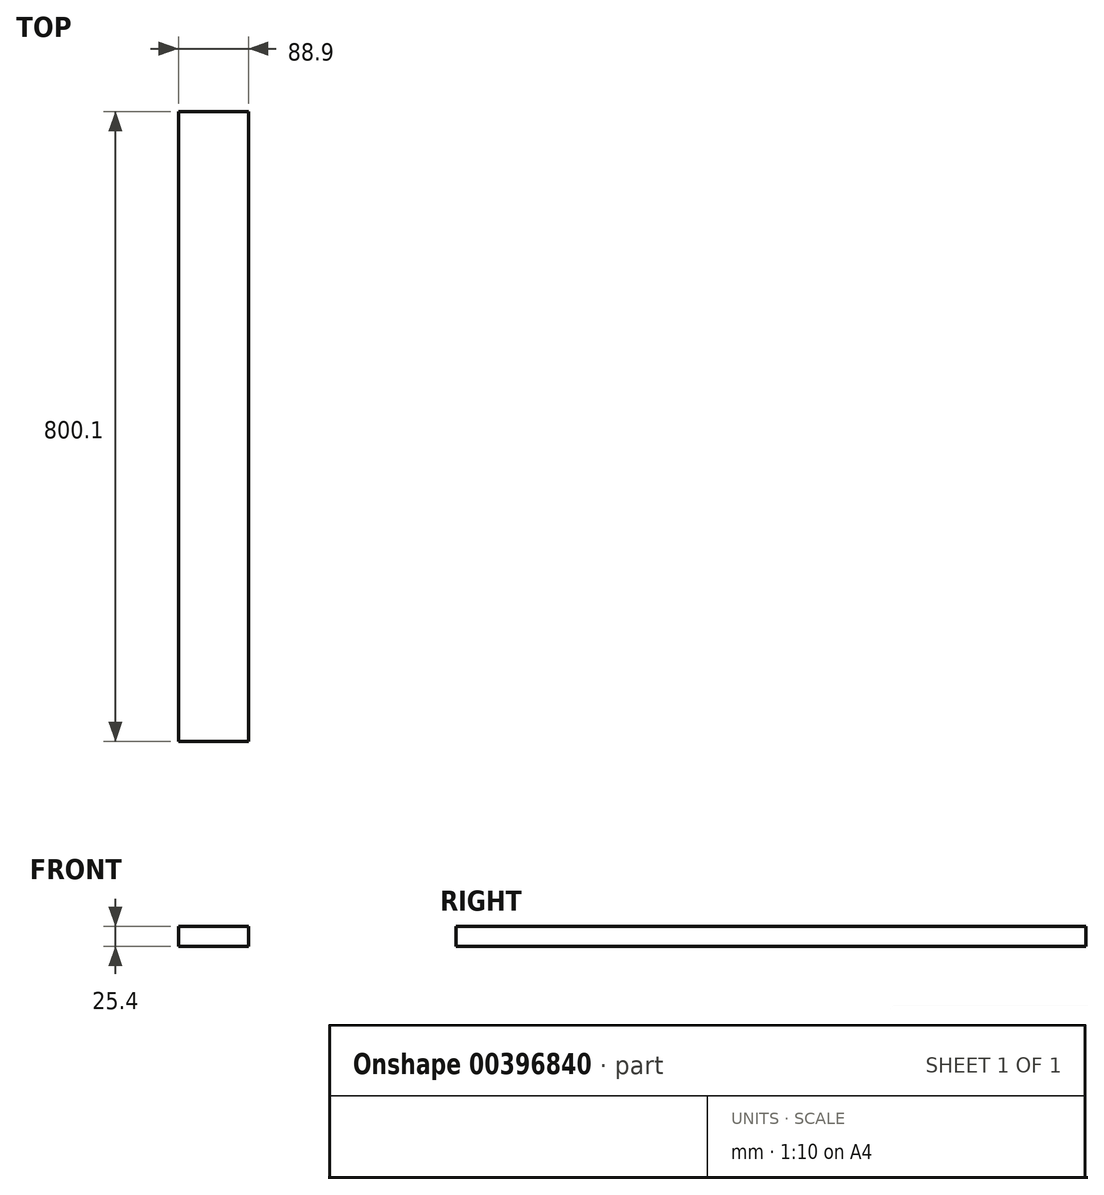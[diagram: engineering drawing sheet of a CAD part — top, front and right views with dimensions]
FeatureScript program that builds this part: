
annotation { "Feature Type Name" : "Feature", "Feature Type Description" : "" }
export const myFeature = defineFeature(function(context is Context, id is Id, definition is map)
    precondition{}
    {
        {
            var Q0;
            Q0=qCreatedBy(makeId("Top.planeOp"),FACE);
            var sketch = newSketch(context, id + "F0", { "sketchPlane" : qUnion([Q0])});
            skLineSegment(sketch, "E0.bottom", {"start": v(-44.45, 400.05) * mm, "end": v(44.45, 400.05) * mm});
            skLineSegment(sketch, "E0.top", {"start": v(-44.45, -400.05) * mm, "end": v(44.45, -400.05) * mm});
            skLineSegment(sketch, "E0.left", {"start": v(-44.45, 400.05) * mm, "end": v(-44.45, -400.05) * mm});
            skLineSegment(sketch, "E0.right", {"start": v(44.45, 400.05) * mm, "end": v(44.45, -400.05) * mm});
            skPoint(sketch, "E0.middle", {"position": v(0, 0) * mm});
            skSolve(sketch);
        }
        {
            var Q0;
            Q0=makeQuery(id+"F0.imprint","IMPRINT",FACE,{"disambiguationData":[TD([[makeQuery(id+"F0.imprint","IMPRINT",EDGE,{"derivedFrom":sQuery(id+"F0.wireOp",EDGE,"E0.bottom")}),-1.0]])]});
            extrude(context, id + "F1", {"entities" : qUnion([Q0]), "depth" : 25.4 * mm});
        }
    });
